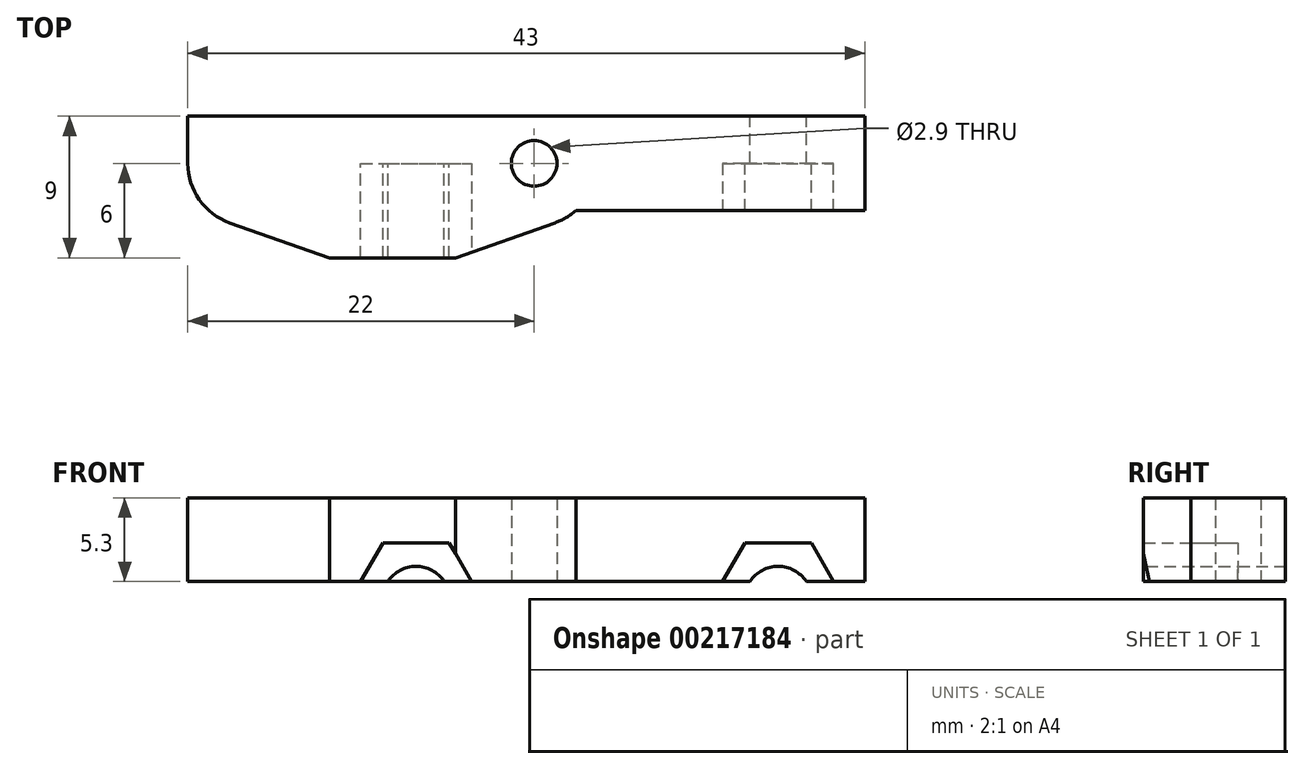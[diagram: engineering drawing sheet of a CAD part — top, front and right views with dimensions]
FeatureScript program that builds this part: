
annotation { "Feature Type Name" : "Feature", "Feature Type Description" : "" }
export const myFeature = defineFeature(function(context is Context, id is Id, definition is map)
    precondition{}
    {
        {
            var Q0;
            Q0=qCreatedBy(makeId("Top.planeOp"),FACE);
            var sketch = newSketch(context, id + "F0", { "sketchPlane" : qUnion([Q0])});
            skLineSegment(sketch, "E0", {"start": v(17, 3) * mm, "end": v(-26, 3) * mm});
            skLineSegment(sketch, "E1", {"start": v(17, 3) * mm, "end": v(17, -3) * mm});
            skLineSegment(sketch, "E2", {"start": v(-17, -6) * mm, "end": v(-9, -6) * mm});
            skLineSegment(sketch, "E3", {"start": v(-26, 3) * mm, "end": v(-26, 0) * mm});
            skArc(sketch, "E4", {"start": v(-26, 0) * mm, "mid": v(-25.26, -2.31) * mm, "end": v(-23.33, -3.77) * mm});
            skCircle(sketch, "E5", {"center": v(-22, 0) * mm, "radius": 1.45 * mm});
            skPoint(sketch, "E6", {"position": v(-13, -6) * mm});
            skLineSegment(sketch, "E7", {"start": v(-13, -6) * mm, "end": v(-13, 0.93) * mm, "construction": true});
            skLineSegment(sketch, "E8", {"start": v(-23.33, -3.77) * mm, "end": v(-17, -6) * mm});
            skArc(sketch, "E9.MirrorCS", {"start": v(-1.35, -3) * mm, "mid": v(-1.98, -3.45) * mm, "end": v(-2.67, -3.77) * mm});
            skLineSegment(sketch, "E10.MirrorCS", {"start": v(-2.67, -3.77) * mm, "end": v(-9, -6) * mm});
            skCircle(sketch, "E11.MirrorC", {"center": v(-4, 0) * mm, "radius": 1.45 * mm});
            skLineSegment(sketch, "E12", {"start": v(17, -3) * mm, "end": v(-1.35, -3) * mm});
            skPoint(sketch, "E13.orphan", {"position": v(0, 0) * mm});
            skSolve(sketch);
        }
        {
            var Q0;
            Q0=makeQuery(id+"F0.imprint","IMPRINT",FACE,{"disambiguationData":[TD([[makeQuery(id+"F0.imprint","IMPRINT",EDGE,{"derivedFrom":sQuery(id+"F0.wireOp",EDGE,"E0")}),1.0]])]});
            var Q1;
            Q1=makeQuery(id+"F0.imprint","IMPRINT",FACE,{"disambiguationData":[TD([[makeQuery(id+"F0.imprint","IMPRINT",EDGE,{"derivedFrom":sQuery(id+"F0.wireOp",EDGE,"E5")}),1.0]])]});
            var Q2;
            Q2=makeQuery(id+"F0.imprint","IMPRINT",FACE,{"disambiguationData":[TD([[makeQuery(id+"F0.imprint","IMPRINT",EDGE,{"derivedFrom":sQuery(id+"F0.wireOp",EDGE,"E11.MirrorC")}),-1.0]])]});
            extrude(context, id + "F1", {"entities" : qUnion([Q0, Q1, Q2]), "depth" : 13 * mm, "offsetDistance" : 25 * mm});
        }
        {
            var Q0;
            Q0=makeQuery(id+"F1.opExtrude","SWEPT_FACE",FACE,{"disambiguationData":[OSD([sQuery(id+"F0.wireOp",EDGE,"E0")])]});
            var sketch = newSketch(context, id + "F2", { "sketchPlane" : qUnion([Q0])});
            skCircle(sketch, "E14", {"center": v(-11.5, 6.5) * mm, "radius": 2.15 * mm});
            skPoint(sketch, "E14.centerSnap0", {"position": v(-17, 6.5) * mm});
            skCircle(sketch, "E15.cCircle", {"center": v(-11.5, 6.5) * mm, "radius": 3.65 * mm, "construction": true});
            skLineSegment(sketch, "E15.0", {"start": v(-13.6, 10.15) * mm, "end": v(-9.4, 10.15) * mm});
            skLineSegment(sketch, "E15.1", {"start": v(-9.4, 10.15) * mm, "end": v(-7.29, 6.5) * mm});
            skLineSegment(sketch, "E15.2", {"start": v(-7.29, 6.5) * mm, "end": v(-9.4, 2.85) * mm});
            skLineSegment(sketch, "E15.3", {"start": v(-9.4, 2.85) * mm, "end": v(-13.6, 2.85) * mm});
            skLineSegment(sketch, "E15.4", {"start": v(-13.6, 2.85) * mm, "end": v(-15.71, 6.5) * mm});
            skLineSegment(sketch, "E15.5", {"start": v(-15.71, 6.5) * mm, "end": v(-13.6, 10.15) * mm});
            skPoint(sketch, "E15.0.midPoint", {"position": v(-11.5, 10.15) * mm});
            skLineSegment(sketch, "E16.MirrorCS", {"start": v(9.4, 2.85) * mm, "end": v(13.6, 2.85) * mm});
            skLineSegment(sketch, "E17.MirrorCS", {"start": v(7.29, 6.5) * mm, "end": v(9.4, 2.85) * mm});
            skLineSegment(sketch, "E18.MirrorCS", {"start": v(9.4, 10.15) * mm, "end": v(7.29, 6.5) * mm});
            skCircle(sketch, "E19.MirrorC", {"center": v(11.5, 6.5) * mm, "radius": 3.65 * mm, "construction": true});
            skLineSegment(sketch, "E20.MirrorCS", {"start": v(15.71, 6.5) * mm, "end": v(13.6, 10.15) * mm});
            skLineSegment(sketch, "E21.MirrorCS", {"start": v(13.6, 2.85) * mm, "end": v(15.71, 6.5) * mm});
            skCircle(sketch, "E22.MirrorC", {"center": v(11.5, 6.5) * mm, "radius": 2.15 * mm});
            skLineSegment(sketch, "E23.MirrorCS", {"start": v(13.6, 10.15) * mm, "end": v(9.4, 10.15) * mm});
            skPoint(sketch, "E24.MirrorP", {"position": v(11.5, 10.15) * mm});
            skSolve(sketch);
        }
        {
            var Q0;
            Q0=makeQuery(id+"F2.imprint","IMPRINT",FACE,{"disambiguationData":[TD([[makeQuery(id+"F2.imprint","IMPRINT",EDGE,{"derivedFrom":sQuery(id+"F2.wireOp",EDGE,"E14")}),-1.0]])]});
            var Q1;
            Q1=makeQuery(id+"F2.imprint","IMPRINT",FACE,{"disambiguationData":[TD([[makeQuery(id+"F2.imprint","IMPRINT",EDGE,{"derivedFrom":sQuery(id+"F2.wireOp",EDGE,"E14")}),1.0]])]});
            var Q2;
            Q2=makeQuery(id+"F2.imprint","IMPRINT",FACE,{"disambiguationData":[TD([[makeQuery(id+"F2.imprint","IMPRINT",EDGE,{"derivedFrom":sQuery(id+"F2.wireOp",EDGE,"E22.MirrorC")}),-1.0]])]});
            var Q3;
            Q3=makeQuery(id+"F2.imprint","IMPRINT",FACE,{"disambiguationData":[TD([[makeQuery(id+"F2.imprint","IMPRINT",EDGE,{"derivedFrom":sQuery(id+"F2.wireOp",EDGE,"E16.MirrorCS")}),1.0]])]});
            extrude(context, id + "F3", {"entities" : qUnion([Q0, Q1, Q2, Q3]), "operationType" : NewBodyOperationType.REMOVE, "endBound" : BoundingType.THROUGH_ALL, "oppositeDirection" : true, "depth" : 25 * mm, "offsetDistance" : 25 * mm});
        }
        {
            var Q0;
            Q0=makeQuery(id+"F2.imprint","IMPRINT",FACE,{"disambiguationData":[TD([[makeQuery(id+"F2.imprint","IMPRINT",EDGE,{"derivedFrom":sQuery(id+"F2.wireOp",EDGE,"E14")}),-1.0]])]});
            var Q1;
            Q1=makeQuery(id+"F2.imprint","IMPRINT",FACE,{"disambiguationData":[TD([[makeQuery(id+"F2.imprint","IMPRINT",EDGE,{"derivedFrom":sQuery(id+"F2.wireOp",EDGE,"E16.MirrorCS")}),1.0]])]});
            extrude(context, id + "F4", {"entities" : qUnion([Q0, Q1]), "operationType" : NewBodyOperationType.ADD, "oppositeDirection" : true, "depth" : 3 * mm, "offsetDistance" : 25 * mm});
        }
        {
            var Q0;
            Q0=makeQuery(id+"F0.imprint","IMPRINT",FACE,{"disambiguationData":[TD([[makeQuery(id+"F0.imprint","IMPRINT",EDGE,{"derivedFrom":sQuery(id+"F0.wireOp",EDGE,"E11.MirrorC")}),-1.0]])]});
            var Q1;
            Q1=makeQuery(id+"F0.imprint","IMPRINT",FACE,{"disambiguationData":[TD([[makeQuery(id+"F0.imprint","IMPRINT",EDGE,{"derivedFrom":sQuery(id+"F0.wireOp",EDGE,"E5")}),1.0]])]});
            extrude(context, id + "F5", {"entities" : qUnion([Q0, Q1]), "operationType" : NewBodyOperationType.REMOVE, "depth" : 7.7 * mm, "offsetDistance" : 25 * mm});
        }
    });
